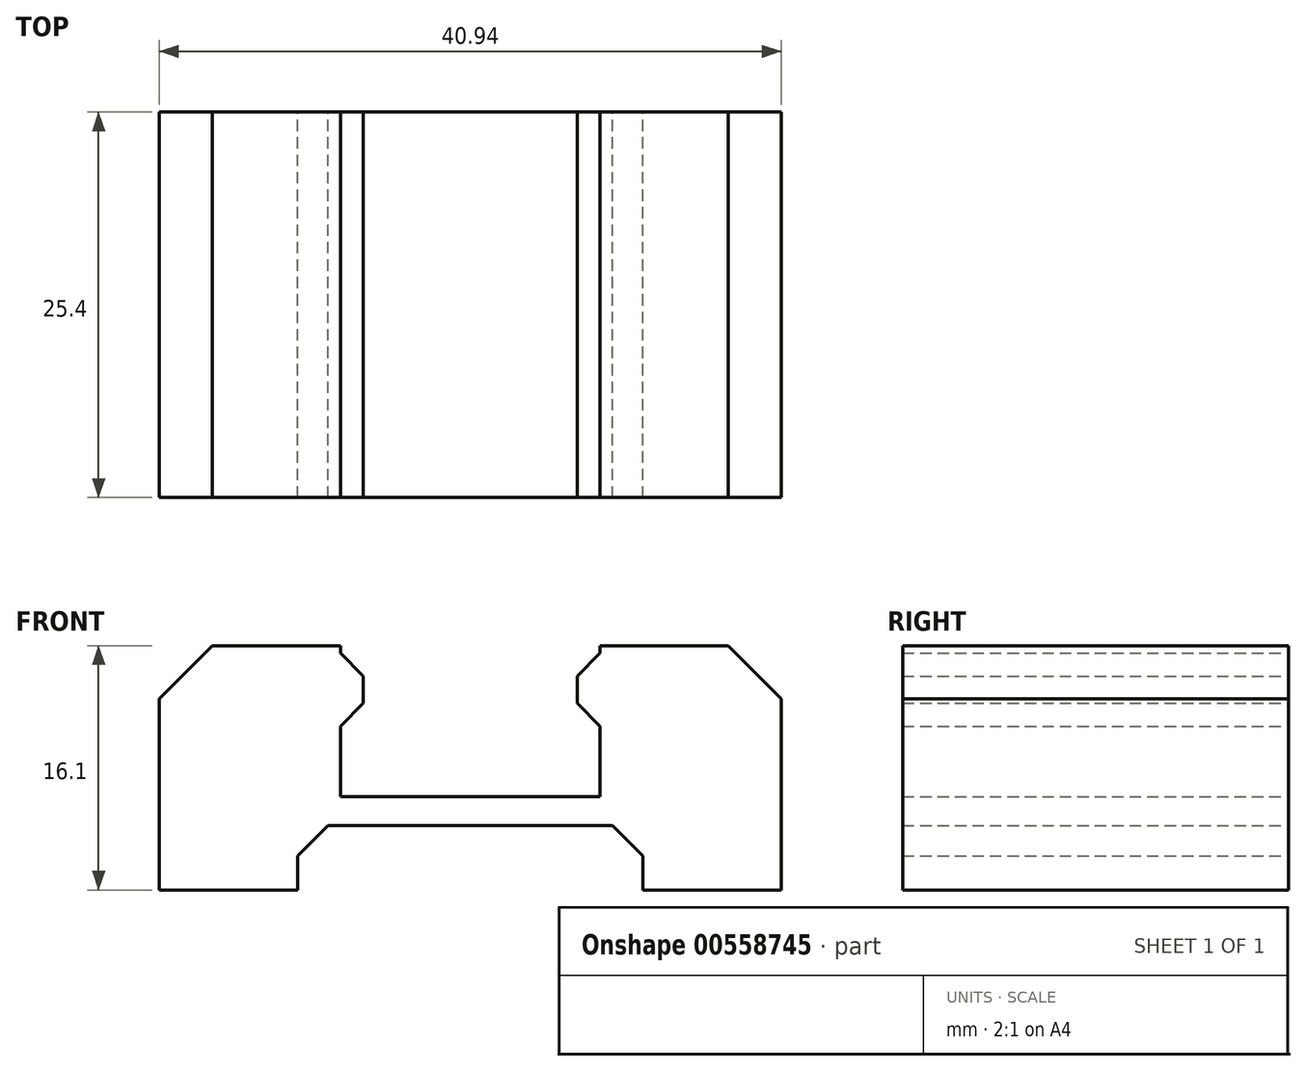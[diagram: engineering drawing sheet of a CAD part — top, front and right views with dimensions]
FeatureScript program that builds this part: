
annotation { "Feature Type Name" : "Feature", "Feature Type Description" : "" }
export const myFeature = defineFeature(function(context is Context, id is Id, definition is map)
    precondition{}
    {
        {
            var Q0;
            Q0=qCreatedBy(makeId("Front.planeOp"),FACE);
            var sketch = newSketch(context, id + "F0", { "sketchPlane" : qUnion([Q0])});
            skLineSegment(sketch, "E0", {"start": v(0, 0) * mm, "end": v(0, 30.92) * mm, "construction": true});
            skLineSegment(sketch, "E1", {"start": v(11.37, 0) * mm, "end": v(11.37, 2.26) * mm});
            skLineSegment(sketch, "E2", {"start": v(8.55, 6.15) * mm, "end": v(8.55, 10.8) * mm});
            skLineSegment(sketch, "E3", {"start": v(16.97, 16.1) * mm, "end": v(20.47, 12.6) * mm});
            skLineSegment(sketch, "E4", {"start": v(11.37, 0) * mm, "end": v(20.47, 0) * mm});
            skLineSegment(sketch, "E5", {"start": v(20.47, 12.6) * mm, "end": v(20.47, 0) * mm});
            skLineSegment(sketch, "E6", {"start": v(7.05, 14.1) * mm, "end": v(7.05, 12.3) * mm});
            skLineSegment(sketch, "E7", {"start": v(7.05, 12.3) * mm, "end": v(8.55, 10.8) * mm});
            skLineSegment(sketch, "E8", {"start": v(7.05, 14.1) * mm, "end": v(8.55, 15.6) * mm});
            skLineSegment(sketch, "E9", {"start": v(8.55, 15.6) * mm, "end": v(8.55, 16.1) * mm});
            skLineSegment(sketch, "E10.MirrorCS", {"start": v(-8.55, 15.6) * mm, "end": v(-8.55, 16.1) * mm});
            skLineSegment(sketch, "E11.MirrorCS", {"start": v(-7.05, 14.1) * mm, "end": v(-8.55, 15.6) * mm});
            skLineSegment(sketch, "E12.MirrorCS", {"start": v(-7.05, 14.1) * mm, "end": v(-7.05, 12.3) * mm});
            skLineSegment(sketch, "E13.MirrorCS", {"start": v(-7.05, 12.3) * mm, "end": v(-8.55, 10.8) * mm});
            skLineSegment(sketch, "E14.MirrorCS", {"start": v(-8.55, 6.15) * mm, "end": v(-8.55, 10.8) * mm});
            skLineSegment(sketch, "E15.MirrorCS", {"start": v(-11.37, 0) * mm, "end": v(-11.37, 2.26) * mm});
            skLineSegment(sketch, "E16.MirrorCS", {"start": v(-16.97, 16.1) * mm, "end": v(-20.47, 12.6) * mm});
            skLineSegment(sketch, "E17.MirrorCS", {"start": v(-20.47, 12.6) * mm, "end": v(-20.47, 0) * mm});
            skLineSegment(sketch, "E18.MirrorCS", {"start": v(-11.37, 0) * mm, "end": v(-20.47, 0) * mm});
            skLineSegment(sketch, "E19", {"start": v(-8.55, 6.15) * mm, "end": v(8.55, 6.15) * mm});
            skLineSegment(sketch, "E20", {"start": v(8.55, 16.1) * mm, "end": v(16.97, 16.1) * mm});
            skLineSegment(sketch, "E21.MirrorCS", {"start": v(-8.55, 16.1) * mm, "end": v(-16.97, 16.1) * mm});
            skLineSegment(sketch, "E22", {"start": v(11.37, 2.26) * mm, "end": v(9.37, 4.26) * mm});
            skLineSegment(sketch, "E23.MirrorCS", {"start": v(-11.37, 2.26) * mm, "end": v(-9.37, 4.26) * mm});
            skLineSegment(sketch, "E24", {"start": v(-9.37, 4.26) * mm, "end": v(9.37, 4.26) * mm});
            skLineSegment(sketch, "E25", {"start": v(0, 0) * mm, "end": v(105.23, 0) * mm, "construction": true});
            skLineSegment(sketch, "E26", {"start": v(11.37, 0) * mm, "end": v(0, 0) * mm, "construction": true});
            skSolve(sketch);
        }
        {
            var Q0;
            Q0 = qSketchRegion(id + "F0", true);
            extrude(context, id + "F1", {"entities" : qUnion([Q0]), "depth" : 25.4 * mm, "offsetDistance" : 25.4 * mm});
        }
    });
